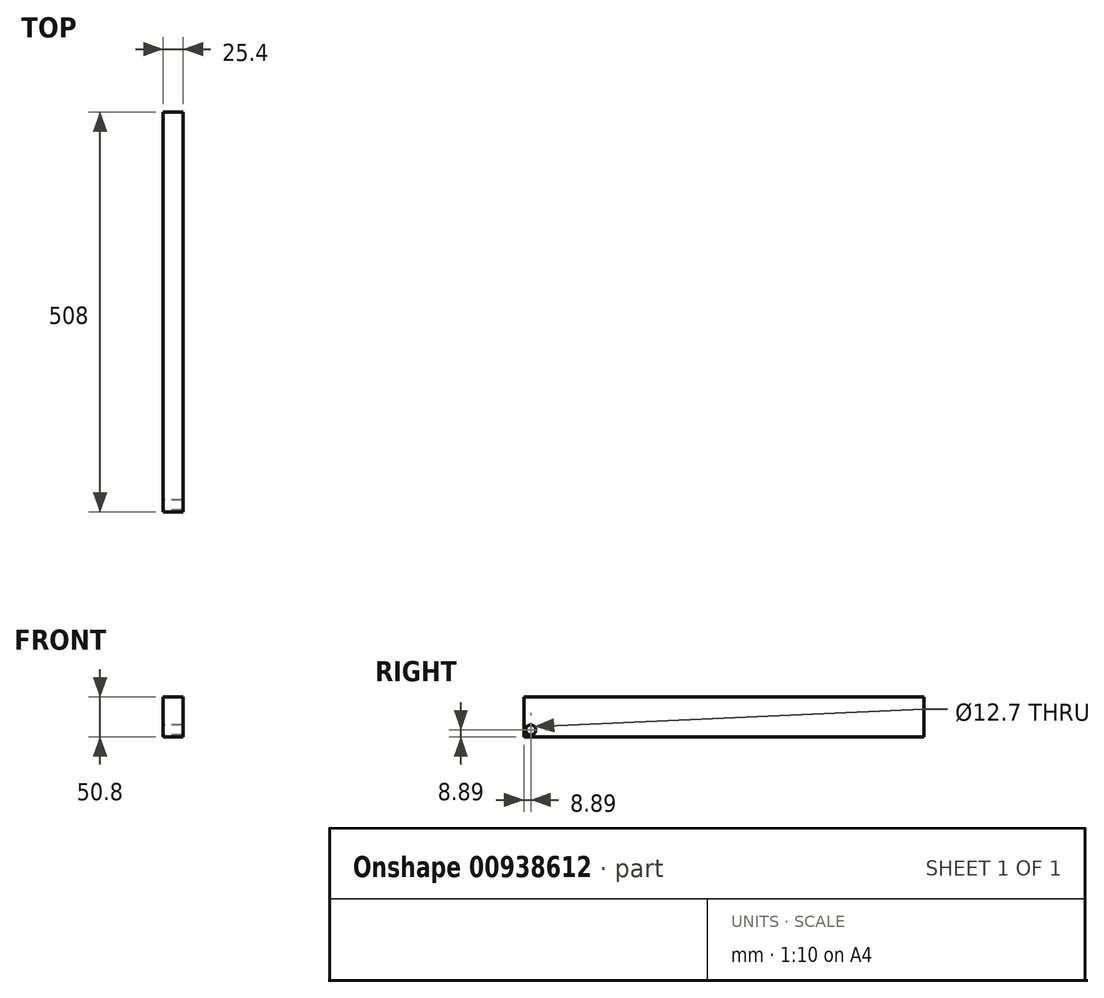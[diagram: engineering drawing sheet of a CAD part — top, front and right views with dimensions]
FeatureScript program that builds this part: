
annotation { "Feature Type Name" : "Feature", "Feature Type Description" : "" }
export const myFeature = defineFeature(function(context is Context, id is Id, definition is map)
    precondition{}
    {
        {
            var Q0;
            Q0=qCreatedBy(makeId("Right.planeOp"),FACE);
            var sketch = newSketch(context, id + "F0", { "sketchPlane" : qUnion([Q0])});
            skLineSegment(sketch, "E0.bottom", {"start": v(-254, 25.4) * mm, "end": v(254, 25.4) * mm});
            skLineSegment(sketch, "E0.top", {"start": v(-254, -25.4) * mm, "end": v(254, -25.4) * mm});
            skLineSegment(sketch, "E0.left", {"start": v(-254, 25.4) * mm, "end": v(-254, -25.4) * mm});
            skLineSegment(sketch, "E0.right", {"start": v(254, 25.4) * mm, "end": v(254, -25.4) * mm});
            skPoint(sketch, "E0.middle", {"position": v(0, 0) * mm});
            skCircle(sketch, "E1", {"center": v(-245.1, -16.5) * mm, "radius": 6.35 * mm});
            skSolve(sketch);
        }
        {
            var Q0;
            Q0 = qSketchRegion(id + "F0", true);
            extrude(context, id + "F1", {"entities" : qUnion([Q0]), "depth" : 25.4 * mm, "offsetDistance" : 25.4 * mm});
        }
    });
